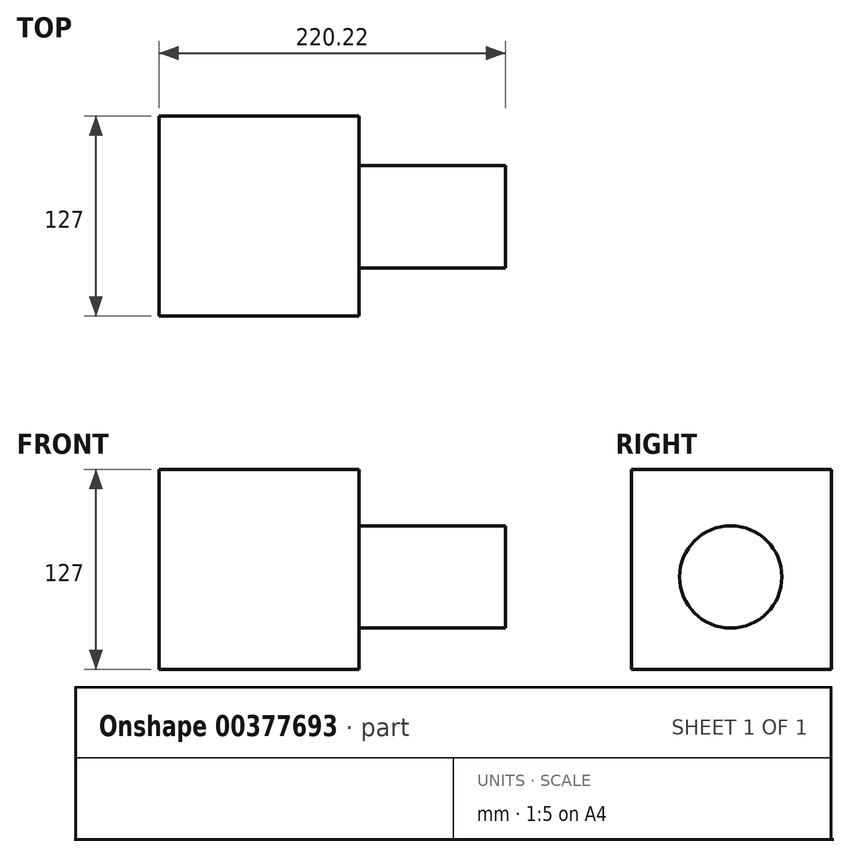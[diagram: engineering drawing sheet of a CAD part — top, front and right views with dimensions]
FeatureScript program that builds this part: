
annotation { "Feature Type Name" : "Feature", "Feature Type Description" : "" }
export const myFeature = defineFeature(function(context is Context, id is Id, definition is map)
    precondition{}
    {
        {
            var Q0;
            Q0=qCreatedBy(makeId("Top.planeOp"),FACE);
            var sketch = newSketch(context, id + "F0", { "sketchPlane" : qUnion([Q0])});
            skLineSegment(sketch, "E0.bottom", {"start": v(-63.5, 0) * mm, "end": v(63.5, 0) * mm});
            skLineSegment(sketch, "E0.top", {"start": v(-63.5, -127) * mm, "end": v(63.5, -127) * mm});
            skLineSegment(sketch, "E0.left", {"start": v(-63.5, 0) * mm, "end": v(-63.5, -127) * mm});
            skLineSegment(sketch, "E0.right", {"start": v(63.5, 0) * mm, "end": v(63.5, -127) * mm});
            skSolve(sketch);
        }
        {
            var Q0;
            Q0 = qSketchRegion(id + "F0", true);
            extrude(context, id + "F1", {"entities" : qUnion([Q0]), "depth" : 127 * mm});
        }
        {
            var Q0;
            Q0=makeQuery(id+"F1.opExtrude","SWEPT_FACE",FACE,{"disambiguationData":[OSD([sQuery(id+"F0.wireOp",EDGE,"E0.right")])]});
            var sketch = newSketch(context, id + "F2", { "sketchPlane" : qUnion([Q0])});
            skCircle(sketch, "E1", {"center": v(-64, 58.81) * mm, "radius": 32.47 * mm});
            skSolve(sketch);
        }
        {
            var Q0;
            Q0 = qSketchRegion(id + "F2", true);
            extrude(context, id + "F3", {"entities" : qUnion([Q0]), "operationType" : NewBodyOperationType.ADD, "depth" : 93.22 * mm});
        }
    });
